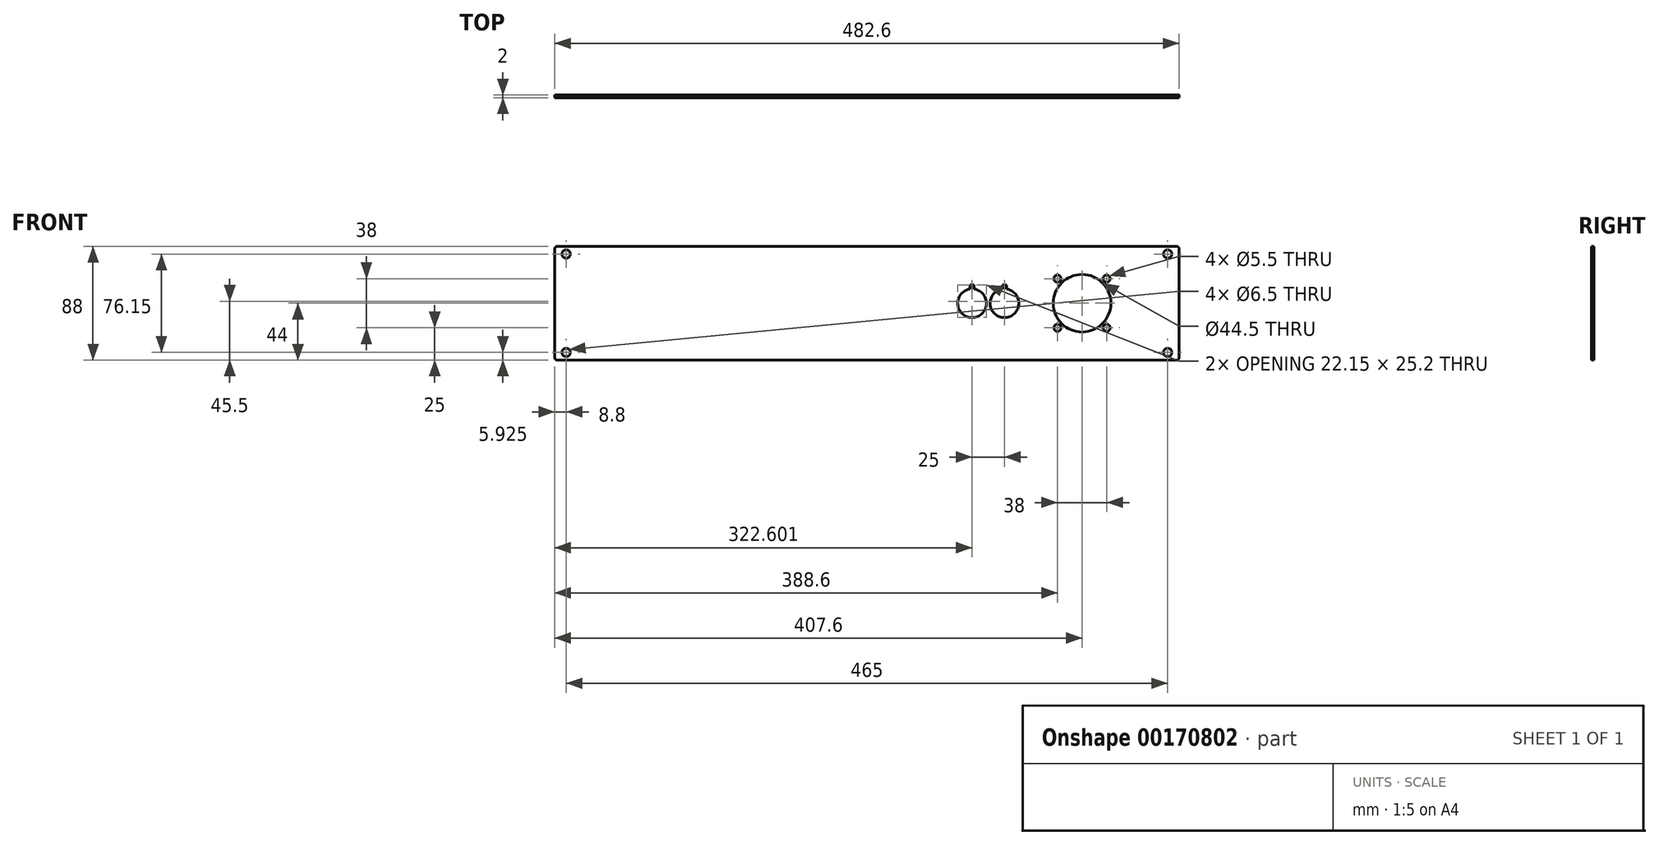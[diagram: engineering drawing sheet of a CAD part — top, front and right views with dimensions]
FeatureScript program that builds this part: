
annotation { "Feature Type Name" : "Feature", "Feature Type Description" : "" }
export const myFeature = defineFeature(function(context is Context, id is Id, definition is map)
    precondition{}
    {
        {
            var Q0;
            Q0=qCreatedBy(makeId("Front.planeOp"),FACE);
            var sketch = newSketch(context, id + "F0", { "sketchPlane" : qUnion([Q0])});
            skLineSegment(sketch, "E0.bottom", {"start": v(241.3, 44) * mm, "end": v(-241.3, 44) * mm});
            skLineSegment(sketch, "E0.top", {"start": v(241.3, -44) * mm, "end": v(-241.3, -44) * mm});
            skLineSegment(sketch, "E0.left", {"start": v(241.3, 44) * mm, "end": v(241.3, -44) * mm});
            skLineSegment(sketch, "E0.right", {"start": v(-241.3, 44) * mm, "end": v(-241.3, -44) * mm});
            skPoint(sketch, "E0.middle", {"position": v(0, 0) * mm});
            skCircle(sketch, "E1", {"center": v(-232.5, -38.08) * mm, "radius": 3.25 * mm});
            skCircle(sketch, "E2", {"center": v(-232.5, 38.08) * mm, "radius": 3.25 * mm});
            skCircle(sketch, "E3.MirrorC", {"center": v(232.5, -38.08) * mm, "radius": 3.25 * mm});
            skCircle(sketch, "E4.MirrorC", {"center": v(232.5, 38.08) * mm, "radius": 3.25 * mm});
            skCircle(sketch, "E5", {"center": v(166.3, 0) * mm, "radius": 22.25 * mm});
            skCircle(sketch, "E6", {"center": v(147.3, 19) * mm, "radius": 2.75 * mm});
            skCircle(sketch, "E7", {"center": v(185.3, 19) * mm, "radius": 2.75 * mm});
            skCircle(sketch, "E8", {"center": v(185.3, -19) * mm, "radius": 2.75 * mm});
            skCircle(sketch, "E9", {"center": v(147.3, -19) * mm, "radius": 2.75 * mm});
            skLineSegment(sketch, "E10.bottom", {"start": v(191.3, 25) * mm, "end": v(141.3, 25) * mm, "construction": true});
            skLineSegment(sketch, "E10.top", {"start": v(191.3, -25) * mm, "end": v(141.3, -25) * mm, "construction": true});
            skLineSegment(sketch, "E10.left", {"start": v(191.3, 25) * mm, "end": v(191.3, -25) * mm, "construction": true});
            skLineSegment(sketch, "E10.right", {"start": v(141.3, 25) * mm, "end": v(141.3, -25) * mm, "construction": true});
            skArc(sketch, "E11", {"start": v(104.79, 11) * mm, "mid": v(106.31, -11.1) * mm, "end": v(107.79, 11) * mm});
            skLineSegment(sketch, "E12.top", {"start": v(107.79, 14.1) * mm, "end": v(104.79, 14.1) * mm});
            skLineSegment(sketch, "E12.left", {"start": v(107.79, 11) * mm, "end": v(107.79, 14.1) * mm});
            skLineSegment(sketch, "E12.right", {"start": v(104.79, 11) * mm, "end": v(104.79, 14.1) * mm});
            skArc(sketch, "E13.1.0.0", {"start": v(79.79, 11) * mm, "mid": v(81.31, -11.1) * mm, "end": v(82.79, 11) * mm});
            skLineSegment(sketch, "E13.1.0.1", {"start": v(82.79, 11) * mm, "end": v(82.79, 14.1) * mm});
            skLineSegment(sketch, "E13.1.0.2", {"start": v(79.79, 11) * mm, "end": v(79.79, 14.1) * mm});
            skLineSegment(sketch, "E13.1.0.3", {"start": v(82.79, 14.1) * mm, "end": v(79.79, 14.1) * mm});
            skLineSegment(sketch, "E13.direction1", {"start": v(106.3, 0) * mm, "end": v(81.3, 0) * mm, "construction": true});
            skSolve(sketch);
        }
        {
            var Q0;
            Q0=makeQuery(id+"F0.imprint","IMPRINT",FACE,{"disambiguationData":[TD([[makeQuery(id+"F0.imprint","IMPRINT",EDGE,{"derivedFrom":sQuery(id+"F0.wireOp",EDGE,"E0.bottom")}),1.0]])]});
            extrude(context, id + "F1", {"entities" : qUnion([Q0]), "endBound" : BoundingType.SYMMETRIC, "depth" : 2 * mm});
        }
        {
            var Q0;
            Q0=makeQuery(id+"F1.opExtrude","SWEPT_EDGE",EDGE,{"disambiguationData":[OSD([sQuery(id+"F0.wireOp",EDGE,"E0.bottom"),sQuery(id+"F0.wireOp",EDGE,"E0.left")])]});
            var Q1;
            Q1=makeQuery(id+"F1.opExtrude","SWEPT_EDGE",EDGE,{"disambiguationData":[OSD([sQuery(id+"F0.wireOp",EDGE,"E0.top"),sQuery(id+"F0.wireOp",EDGE,"E0.left")])]});
            var Q2;
            Q2=makeQuery(id+"F1.opExtrude","SWEPT_EDGE",EDGE,{"disambiguationData":[OSD([sQuery(id+"F0.wireOp",EDGE,"E0.top"),sQuery(id+"F0.wireOp",EDGE,"E0.right")])]});
            var Q3;
            Q3=makeQuery(id+"F1.opExtrude","SWEPT_EDGE",EDGE,{"disambiguationData":[OSD([sQuery(id+"F0.wireOp",EDGE,"E0.bottom"),sQuery(id+"F0.wireOp",EDGE,"E0.right")])]});
            fillet(context, id + "F2", {"entities" : qUnion([Q0, Q1, Q2, Q3]), "radius" : 2 * mm, "tangentPropagation" : true, "allowEdgeOverflow" : false});
        }
    });
